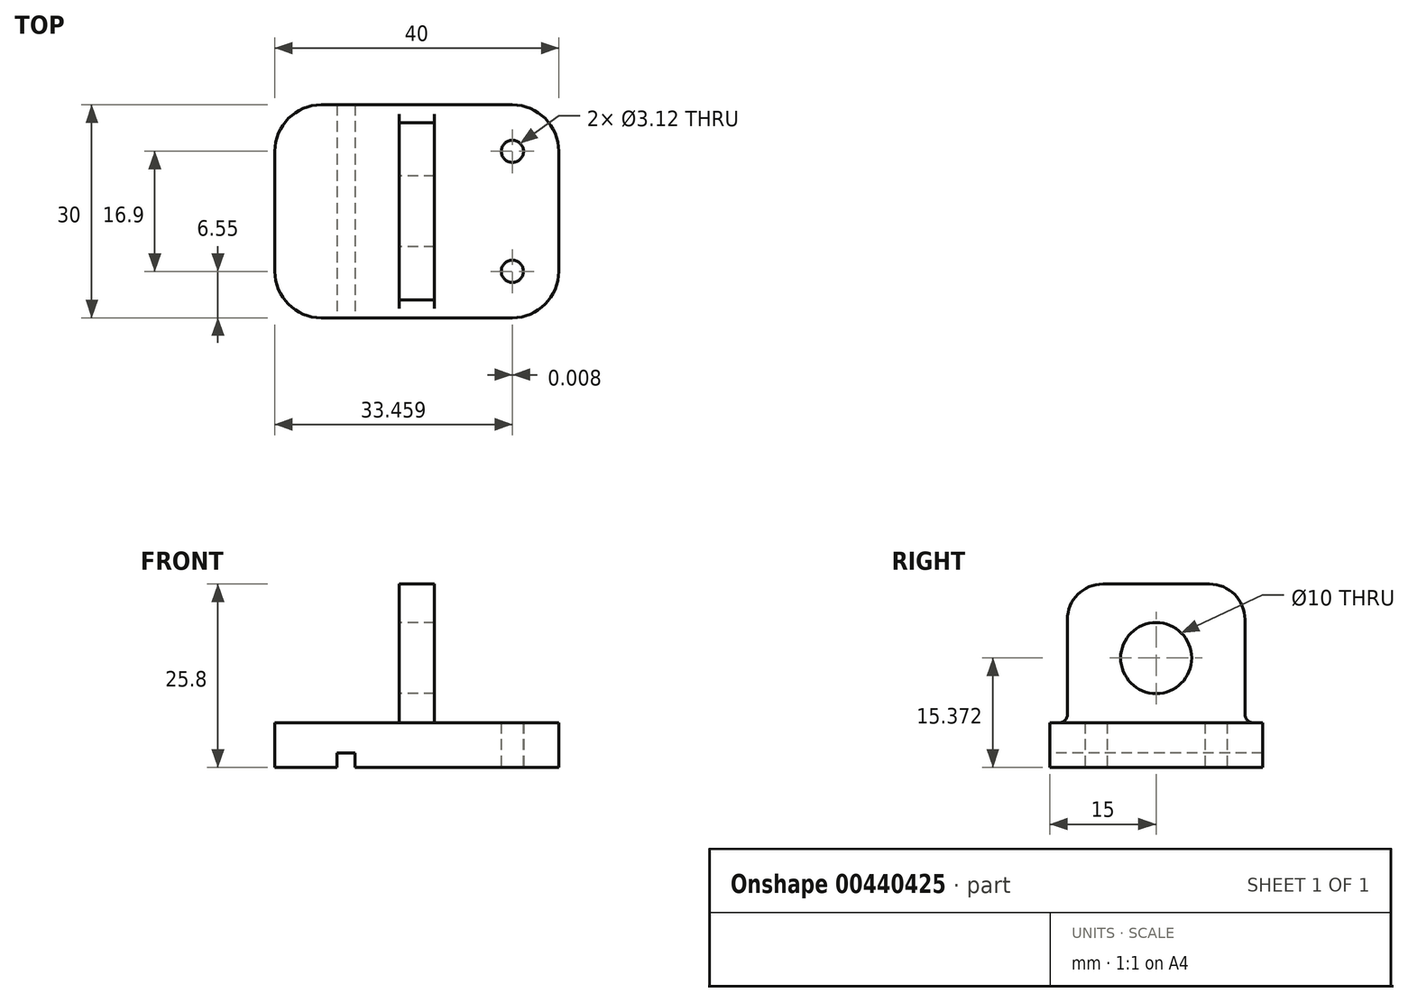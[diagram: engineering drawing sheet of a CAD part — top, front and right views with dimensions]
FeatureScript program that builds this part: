
annotation { "Feature Type Name" : "Feature", "Feature Type Description" : "" }
export const myFeature = defineFeature(function(context is Context, id is Id, definition is map)
    precondition{}
    {
        {
            var Q0;
            Q0=qCreatedBy(makeId("Top.planeOp"),FACE);
            var sketch = newSketch(context, id + "F0", { "sketchPlane" : qUnion([Q0])});
            skLineSegment(sketch, "E0.bottom", {"start": v(20, -15) * mm, "end": v(-20, -15) * mm});
            skLineSegment(sketch, "E0.top", {"start": v(20, 15) * mm, "end": v(-20, 15) * mm});
            skLineSegment(sketch, "E0.left", {"start": v(20, -15) * mm, "end": v(20, 15) * mm});
            skLineSegment(sketch, "E0.right", {"start": v(-20, -15) * mm, "end": v(-20, 15) * mm});
            skPoint(sketch, "E0.middle", {"position": v(0, 0) * mm});
            skLineSegment(sketch, "E1", {"start": v(13.47, -15) * mm, "end": v(13.47, 8.45) * mm, "construction": true});
            skLineSegment(sketch, "E2", {"start": v(13.46, 15) * mm, "end": v(13.46, -8.45) * mm, "construction": true});
            skLineSegment(sketch, "E3", {"start": v(20, 0) * mm, "end": v(13.45, 0) * mm, "construction": true});
            skPoint(sketch, "E3.endSnap0", {"position": v(20, 0) * mm});
            skCircle(sketch, "E4", {"center": v(13.46, -8.45) * mm, "radius": 1.56 * mm});
            skCircle(sketch, "E5", {"center": v(13.47, 8.45) * mm, "radius": 1.56 * mm});
            skSolve(sketch);
        }
        {
            var Q0;
            Q0 = qSketchRegion(id + "F0", true);
            extrude(context, id + "F1", {"entities" : qUnion([Q0]), "depth" : 6.25 * mm});
        }
        {
            var Q0;
            Q0=makeQuery(id+"F1.opExtrude","SWEPT_EDGE",EDGE,{"disambiguationData":[OSD([sQuery(id+"F0.wireOp",EDGE,"E0.bottom"),sQuery(id+"F0.wireOp",EDGE,"E0.right")])]});
            var Q1;
            Q1=makeQuery(id+"F1.opExtrude","SWEPT_EDGE",EDGE,{"disambiguationData":[OSD([sQuery(id+"F0.wireOp",EDGE,"E0.top"),sQuery(id+"F0.wireOp",EDGE,"E0.right")])]});
            var Q2;
            Q2=makeQuery(id+"F1.opExtrude","SWEPT_EDGE",EDGE,{"disambiguationData":[OSD([sQuery(id+"F0.wireOp",EDGE,"E0.bottom"),sQuery(id+"F0.wireOp",EDGE,"E0.left")])]});
            var Q3;
            Q3=makeQuery(id+"F1.opExtrude","SWEPT_EDGE",EDGE,{"disambiguationData":[OSD([sQuery(id+"F0.wireOp",EDGE,"E0.top"),sQuery(id+"F0.wireOp",EDGE,"E0.left")])]});
            fillet(context, id + "F2", {"entities" : qUnion([Q0, Q1, Q2, Q3]), "radius" : 6.55 * mm, "tangentPropagation" : true, "allowEdgeOverflow" : false});
        }
        {
            var Q0;
            Q0=qCreatedBy(makeId("Top.planeOp"),FACE);
            cPlane(context, id + "F3", {"entities" : qUnion([Q0]), "cplaneType" : CPlaneType.OFFSET, "offset" : 5.8 * mm, "width" : 150 * mm, "height" : 150 * mm});
        }
        {
            var Q0;
            Q0=qCreatedBy(id+"F3.planeOp",FACE);
            var sketch = newSketch(context, id + "F4", { "sketchPlane" : qUnion([Q0])});
            skLineSegment(sketch, "E6.bottom", {"start": v(-2.5, 12.5) * mm, "end": v(2.5, 12.5) * mm});
            skLineSegment(sketch, "E6.top", {"start": v(-2.5, -12.5) * mm, "end": v(2.5, -12.5) * mm});
            skLineSegment(sketch, "E6.left", {"start": v(-2.5, 12.5) * mm, "end": v(-2.5, -12.5) * mm});
            skLineSegment(sketch, "E6.right", {"start": v(2.5, 12.5) * mm, "end": v(2.5, -12.5) * mm});
            skPoint(sketch, "E6.middle", {"position": v(0, 0) * mm});
            skLineSegment(sketch, "E7", {"start": v(-20.05, 0) * mm, "end": v(-0.05, 0) * mm, "construction": true});
            skSolve(sketch);
        }
        {
            var Q0;
            Q0 = qSketchRegion(id + "F4", true);
            extrude(context, id + "F5", {"entities" : qUnion([Q0]), "operationType" : NewBodyOperationType.ADD, "depth" : 20 * mm});
        }
        {
            var Q0;
            Q0=makeQuery(id+"F5.opExtrude","CAP_EDGE",EDGE,{"disambiguationData":[OSD([sQuery(id+"F4.wireOp",EDGE,"E6.bottom")])],"isStart":false});
            var Q1;
            Q1=makeQuery(id+"F5.opExtrude","CAP_EDGE",EDGE,{"disambiguationData":[OSD([sQuery(id+"F4.wireOp",EDGE,"E6.top")])],"isStart":false});
            fillet(context, id + "F6", {"entities" : qUnion([Q0, Q1]), "radius" : 5 * mm, "tangentPropagation" : true, "allowEdgeOverflow" : false});
        }
        {
            var Q0;
            Q0=makeQuery(id+"F5.boolean.opBoolean","INTERSECT",EDGE,{"derivedFrom":[makeQuery(id+"F1.opExtrude","CAP_FACE",FACE,{"disambiguationData":[OSD([sQuery(id+"F0.wireOp",EDGE,"E0.bottom"),sQuery(id+"F0.wireOp",EDGE,"E0.top"),sQuery(id+"F0.wireOp",EDGE,"E0.left"),sQuery(id+"F0.wireOp",EDGE,"E0.right"),sQuery(id+"F0.wireOp",EDGE,"E4"),sQuery(id+"F0.wireOp",EDGE,"E5")])],"isStart":false}),makeQuery(id+"F5.opExtrude","SWEPT_FACE",FACE,{"disambiguationData":[OSD([sQuery(id+"F4.wireOp",EDGE,"E6.top")])]})]});
            var Q1;
            Q1=makeQuery(id+"F5.boolean.opBoolean","INTERSECT",EDGE,{"derivedFrom":[makeQuery(id+"F1.opExtrude","CAP_FACE",FACE,{"disambiguationData":[OSD([sQuery(id+"F0.wireOp",EDGE,"E0.bottom"),sQuery(id+"F0.wireOp",EDGE,"E0.top"),sQuery(id+"F0.wireOp",EDGE,"E0.left"),sQuery(id+"F0.wireOp",EDGE,"E0.right"),sQuery(id+"F0.wireOp",EDGE,"E4"),sQuery(id+"F0.wireOp",EDGE,"E5")])],"isStart":false}),makeQuery(id+"F5.opExtrude","SWEPT_FACE",FACE,{"disambiguationData":[OSD([sQuery(id+"F4.wireOp",EDGE,"E6.bottom")])]})]});
            fillet(context, id + "F7", {"entities" : qUnion([Q0, Q1]), "radius" : 1.2 * mm, "tangentPropagation" : true, "allowEdgeOverflow" : false});
        }
        {
            var Q0;
            Q0=qCreatedBy(makeId("Front.planeOp"),FACE);
            cPlane(context, id + "F8", {"entities" : qUnion([Q0]), "cplaneType" : CPlaneType.OFFSET, "offset" : 15.1 * mm, "width" : 150 * mm, "height" : 150 * mm});
        }
        {
            var Q0;
            Q0=qCreatedBy(id+"F8.planeOp",FACE);
            var sketch = newSketch(context, id + "F9", { "sketchPlane" : qUnion([Q0])});
            skPoint(sketch, "E8.orphan", {"position": v(-26.55, 0) * mm});
            skPoint(sketch, "E9.start.orphan", {"position": v(-24.42, 0) * mm});
            skLineSegment(sketch, "E10", {"start": v(-19.94, 0) * mm, "end": v(-11.23, 0) * mm, "construction": true});
            skLineSegment(sketch, "E11", {"start": v(-11.23, 0) * mm, "end": v(-11.23, 2) * mm});
            skLineSegment(sketch, "E12", {"start": v(-11.23, 2) * mm, "end": v(-8.73, 2) * mm});
            skLineSegment(sketch, "E13", {"start": v(-8.73, 2) * mm, "end": v(-8.73, 0) * mm});
            skLineSegment(sketch, "E14", {"start": v(-11.23, 0) * mm, "end": v(-8.73, 0) * mm});
            skSolve(sketch);
        }
        {
            var Q0;
            Q0 = qSketchRegion(id + "F9", true);
            extrude(context, id + "F10", {"entities" : qUnion([Q0]), "operationType" : NewBodyOperationType.REMOVE, "oppositeDirection" : true, "depth" : 36 * mm});
        }
        {
            var Q0;
            Q0=qCreatedBy(makeId("Right.planeOp"),FACE);
            var sketch = newSketch(context, id + "F11", { "sketchPlane" : qUnion([Q0])});
            skCircle(sketch, "E15", {"center": v(0, 15.37) * mm, "radius": 5 * mm});
            skSolve(sketch);
        }
        {
            var Q0;
            Q0 = qSketchRegion(id + "F11", true);
            extrude(context, id + "F12", {"entities" : qUnion([Q0]), "operationType" : NewBodyOperationType.REMOVE, "endBound" : BoundingType.SYMMETRIC, "depth" : 31 * mm});
        }
    });
